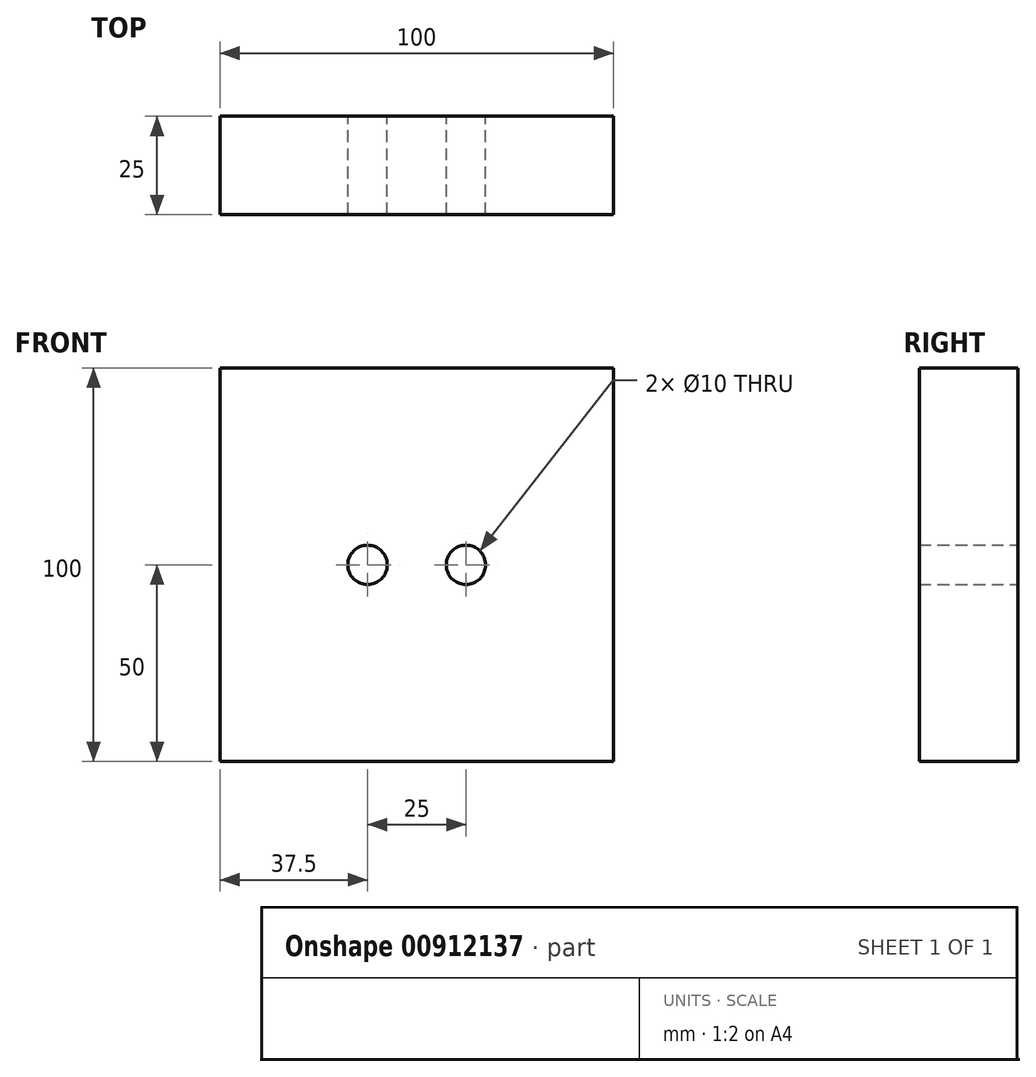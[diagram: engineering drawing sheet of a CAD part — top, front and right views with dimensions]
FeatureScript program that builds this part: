
annotation { "Feature Type Name" : "Feature", "Feature Type Description" : "" }
export const myFeature = defineFeature(function(context is Context, id is Id, definition is map)
    precondition{}
    {
        {
            var Q0;
            Q0=qCreatedBy(makeId("Front.planeOp"),FACE);
            var sketch = newSketch(context, id + "F0", { "sketchPlane" : qUnion([Q0])});
            skLineSegment(sketch, "E0.bottom", {"start": v(-50, 50) * mm, "end": v(50, 50) * mm});
            skLineSegment(sketch, "E0.top", {"start": v(-50, -50) * mm, "end": v(50, -50) * mm});
            skLineSegment(sketch, "E0.left", {"start": v(-50, 50) * mm, "end": v(-50, -50) * mm});
            skLineSegment(sketch, "E0.right", {"start": v(50, 50) * mm, "end": v(50, -50) * mm});
            skCircle(sketch, "E1", {"center": v(-12.5, 0) * mm, "radius": 5 * mm});
            skCircle(sketch, "E2", {"center": v(12.5, 0) * mm, "radius": 5 * mm});
            skSolve(sketch);
        }
        {
            var Q0;
            Q0=makeQuery(id+"F0.imprint","IMPRINT",FACE,{"disambiguationData":[TD([[makeQuery(id+"F0.imprint","IMPRINT",EDGE,{"derivedFrom":sQuery(id+"F0.wireOp",EDGE,"E0.bottom")}),-1.0]])]});
            extrude(context, id + "F1", {"entities" : qUnion([Q0]), "depth" : 25 * mm, "offsetDistance" : 25 * mm});
        }
    });
